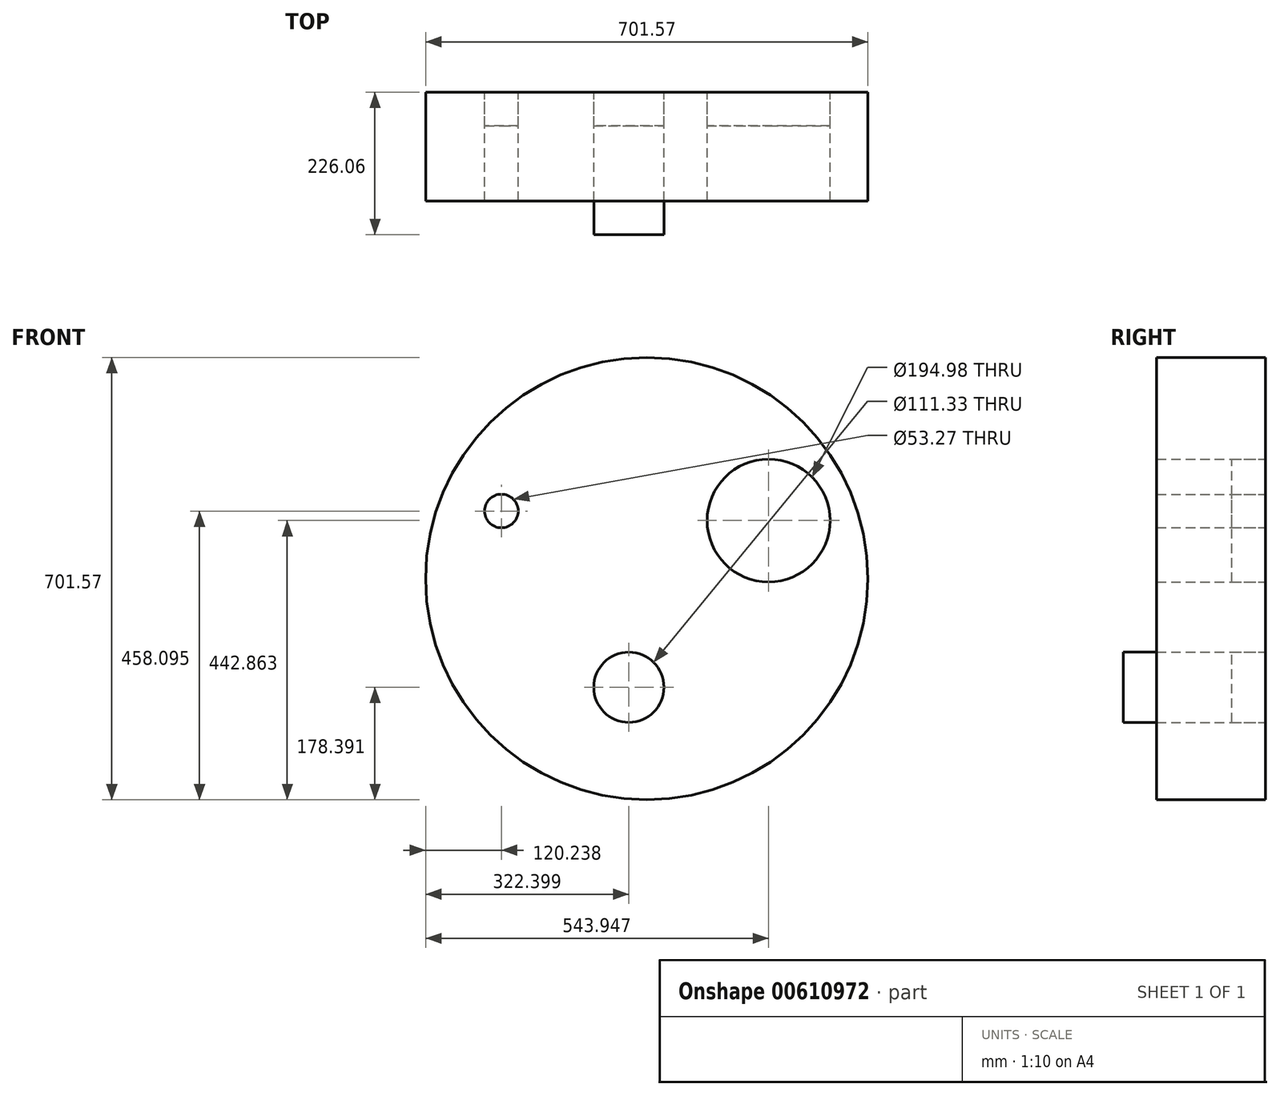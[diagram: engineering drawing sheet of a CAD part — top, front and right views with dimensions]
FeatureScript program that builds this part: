
annotation { "Feature Type Name" : "Feature", "Feature Type Description" : "" }
export const myFeature = defineFeature(function(context is Context, id is Id, definition is map)
    precondition{}
    {
        {
            var Q0;
            Q0=qCreatedBy(makeId("Front.planeOp"),FACE);
            var sketch = newSketch(context, id + "F0", { "sketchPlane" : qUnion([Q0])});
            skCircle(sketch, "E0", {"center": v(-120.4, -41.45) * mm, "radius": 350.78 * mm});
            skCircle(sketch, "E1", {"center": v(72.77, 50.63) * mm, "radius": 97.49 * mm});
            skCircle(sketch, "E2", {"center": v(-148.78, -213.84) * mm, "radius": 55.66 * mm});
            skCircle(sketch, "E3", {"center": v(-350.94, 65.86) * mm, "radius": 26.63 * mm});
            skSolve(sketch);
        }
        {
            var Q0;
            Q0=makeQuery(id+"F0.imprint","IMPRINT",FACE,{"disambiguationData":[TD([[makeQuery(id+"F0.imprint","IMPRINT",EDGE,{"derivedFrom":sQuery(id+"F0.wireOp",EDGE,"E1")}),1.0]])]});
            var Q1;
            Q1=makeQuery(id+"F0.imprint","IMPRINT",FACE,{"disambiguationData":[TD([[makeQuery(id+"F0.imprint","IMPRINT",EDGE,{"derivedFrom":sQuery(id+"F0.wireOp",EDGE,"E3")}),1.0]])]});
            var Q2;
            Q2=makeQuery(id+"F0.imprint","IMPRINT",FACE,{"disambiguationData":[TD([[makeQuery(id+"F0.imprint","IMPRINT",EDGE,{"derivedFrom":sQuery(id+"F0.wireOp",EDGE,"E2")}),1.0]])]});
            extrude(context, id + "F1", {"entities" : qUnion([Q0, Q1, Q2]), "depth" : 53.34 * mm, "offsetDistance" : 25.4 * mm});
        }
        {
            var Q0;
            Q0=makeQuery(id+"F0.imprint","IMPRINT",FACE,{"disambiguationData":[TD([[makeQuery(id+"F0.imprint","IMPRINT",EDGE,{"derivedFrom":sQuery(id+"F0.wireOp",EDGE,"E0")}),1.0]])]});
            var Q1;
            Q1=makeQuery(id+"F1.opExtrude","CAP_FACE",FACE,{"disambiguationData":[OSD([sQuery(id+"F0.wireOp",EDGE,"E2")])],"isStart":false});
            extrude(context, id + "F2", {"entities" : qUnion([Q0, Q1]), "depth" : 172.72 * mm, "offsetDistance" : 25.4 * mm});
        }
    });
